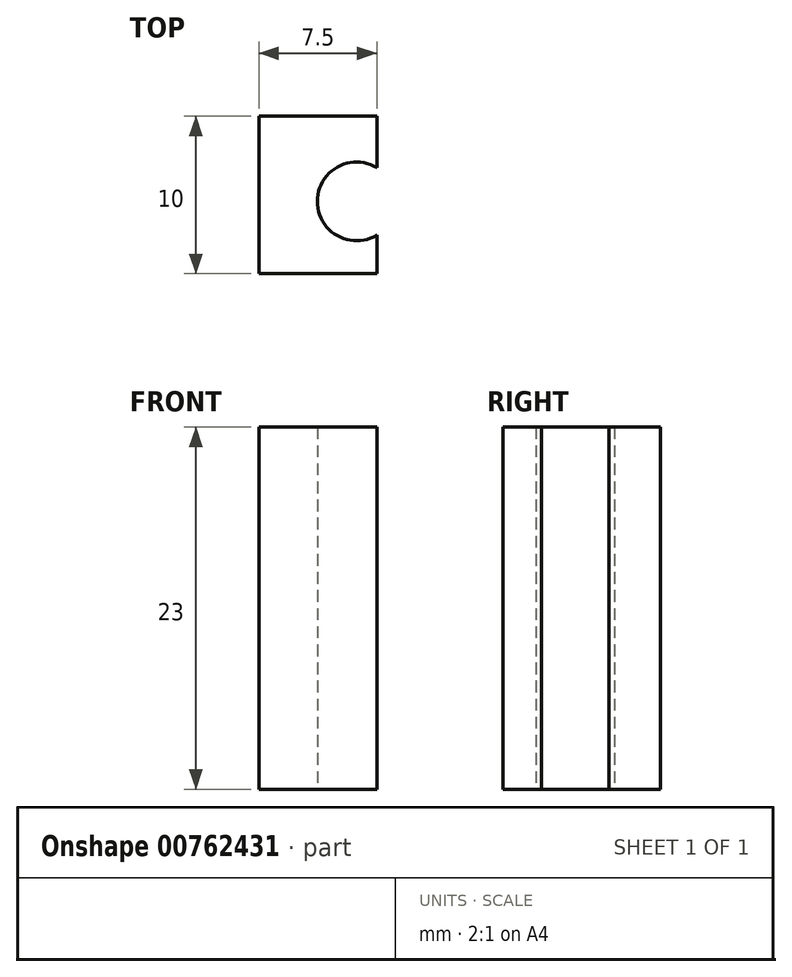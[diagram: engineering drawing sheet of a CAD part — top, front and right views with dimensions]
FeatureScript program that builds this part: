
annotation { "Feature Type Name" : "Feature", "Feature Type Description" : "" }
export const myFeature = defineFeature(function(context is Context, id is Id, definition is map)
    precondition{}
    {
        {
            var Q0;
            Q0=qCreatedBy(makeId("Top.planeOp"),FACE);
            var sketch = newSketch(context, id + "F0", { "sketchPlane" : qUnion([Q0])});
            skLineSegment(sketch, "E0.bottom", {"start": v(-3.75, 5) * mm, "end": v(3.75, 5) * mm});
            skLineSegment(sketch, "E0.top", {"start": v(-3.75, -5) * mm, "end": v(3.75, -5) * mm});
            skLineSegment(sketch, "E0.left", {"start": v(-3.75, 5) * mm, "end": v(-3.75, -5) * mm});
            skLineSegment(sketch, "E0.right", {"start": v(3.75, 5) * mm, "end": v(3.75, -5) * mm});
            skPoint(sketch, "E0.middle", {"position": v(0, 0) * mm});
            skCircle(sketch, "E1", {"center": v(2.47, -0.4) * mm, "radius": 2.5 * mm});
            skPoint(sketch, "E1.first.point", {"position": v(3.27, 1.96) * mm});
            skPoint(sketch, "E1.second.point", {"position": v(0, -0.82) * mm});
            skSolve(sketch);
        }
        {
            var Q0;
            {var subQ1=sQuery(id+"F0.wireOp",EDGE,"E0.bottom");Q0=makeQuery(id+"F0.imprint","IMPRINT",FACE,{"disambiguationData":[TD([[makeQuery(id+"F0.imprint","IMPRINT",EDGE,{"derivedFrom":subQ1}),-1.0]])]});}
            extrude(context, id + "F1", {"entities" : qUnion([Q0]), "depth" : 23 * mm, "offsetDistance" : 25.4 * mm});
        }
    });
